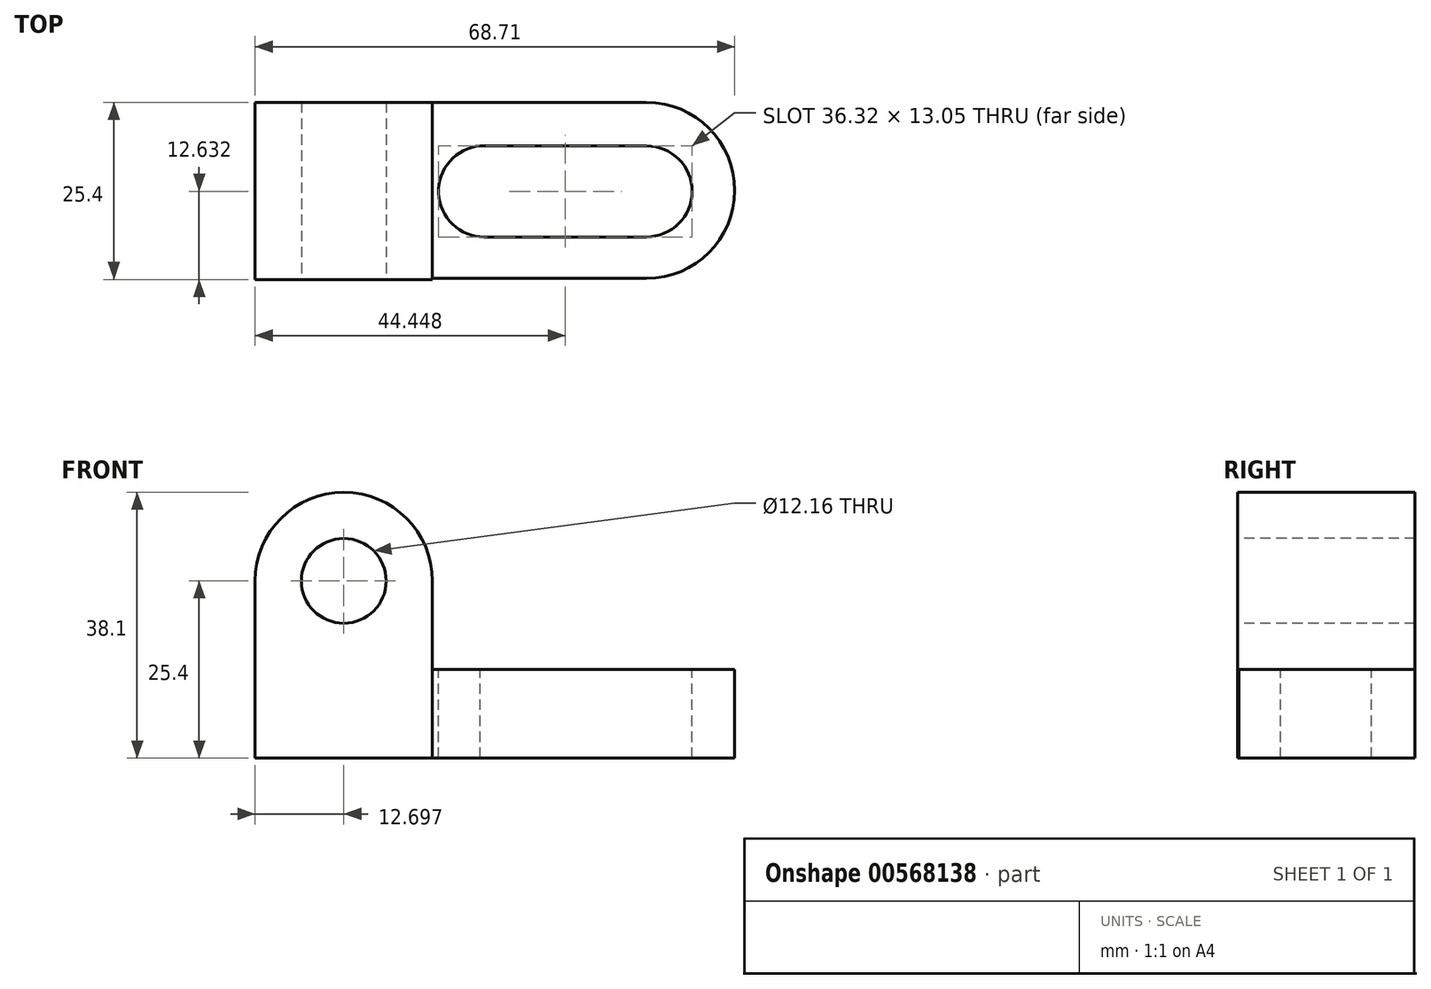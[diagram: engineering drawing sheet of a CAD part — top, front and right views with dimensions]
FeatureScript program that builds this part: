
annotation { "Feature Type Name" : "Feature", "Feature Type Description" : "" }
export const myFeature = defineFeature(function(context is Context, id is Id, definition is map)
    precondition{}
    {
        {
            var Q0;
            Q0=qCreatedBy(makeId("Front.planeOp"),FACE);
            var sketch = newSketch(context, id + "F0", { "sketchPlane" : qUnion([Q0])});
            skLineSegment(sketch, "E0", {"start": v(-70.27, 0) * mm, "end": v(-44.87, 0) * mm});
            skLineSegment(sketch, "E1", {"start": v(-44.87, 0) * mm, "end": v(-44.87, 25.4) * mm});
            skLineSegment(sketch, "E2", {"start": v(-44.87, 25.4) * mm, "end": v(-70.27, 25.4) * mm});
            skLineSegment(sketch, "E3", {"start": v(-70.27, 25.4) * mm, "end": v(-70.27, 0) * mm});
            skArc(sketch, "E4", {"start": v(-44.87, 25.4) * mm, "mid": v(-57.57, 38.1) * mm, "end": v(-70.27, 25.4) * mm});
            skSolve(sketch);
        }
        {
            var Q0;
            Q0=makeQuery(id+"F0.imprint","IMPRINT",FACE,{"disambiguationData":[TD([[makeQuery(id+"F0.imprint","IMPRINT",EDGE,{"derivedFrom":sQuery(id+"F0.wireOp",EDGE,"E0")}),1.0]])]});
            var Q1;
            Q1=makeQuery(id+"F0.imprint","IMPRINT",FACE,{"disambiguationData":[TD([[makeQuery(id+"F0.imprint","IMPRINT",EDGE,{"derivedFrom":sQuery(id+"F0.wireOp",EDGE,"E2")}),-1.0]])]});
            extrude(context, id + "F1", {"entities" : qUnion([Q0, Q1]), "depth" : 25.4 * mm, "offsetDistance" : 25.4 * mm});
        }
        {
            var Q0;
            Q0=qCreatedBy(makeId("Top.planeOp"),FACE);
            var sketch = newSketch(context, id + "F2", { "sketchPlane" : qUnion([Q0])});
            skLineSegment(sketch, "E5", {"start": v(-45.68, 0) * mm, "end": v(-45.68, -25.25) * mm});
            skLineSegment(sketch, "E6", {"start": v(-45.68, -25.25) * mm, "end": v(-14.19, -25.25) * mm});
            skLineSegment(sketch, "E7", {"start": v(-14.19, -25.25) * mm, "end": v(-14.19, 0) * mm});
            skLineSegment(sketch, "E8", {"start": v(-14.19, 0) * mm, "end": v(-45.68, 0) * mm});
            skArc(sketch, "E9", {"start": v(-14.19, -25.25) * mm, "mid": v(-1.56, -12.63) * mm, "end": v(-14.19, 0) * mm});
            skSolve(sketch);
        }
        {
            var Q0;
            Q0=makeQuery(id+"F2.imprint","IMPRINT",FACE,{"disambiguationData":[TD([[makeQuery(id+"F2.imprint","IMPRINT",EDGE,{"derivedFrom":sQuery(id+"F2.wireOp",EDGE,"E5")}),1.0]])]});
            var Q1;
            Q1=makeQuery(id+"F2.imprint","IMPRINT",FACE,{"disambiguationData":[TD([[makeQuery(id+"F2.imprint","IMPRINT",EDGE,{"derivedFrom":sQuery(id+"F2.wireOp",EDGE,"E7")}),-1.0]])]});
            extrude(context, id + "F3", {"entities" : qUnion([Q0, Q1]), "operationType" : NewBodyOperationType.ADD, "depth" : 12.7 * mm, "offsetDistance" : 25.4 * mm});
        }
        {
            var Q0;
            Q0=makeQuery(id+"F1.opExtrude","CAP_FACE",FACE,{"disambiguationData":[OSD([sQuery(id+"F0.wireOp",EDGE,"E0"),sQuery(id+"F0.wireOp",EDGE,"E1"),sQuery(id+"F0.wireOp",EDGE,"E3"),sQuery(id+"F0.wireOp",EDGE,"E4")])],"isStart":false});
            var sketch = newSketch(context, id + "F4", { "sketchPlane" : qUnion([Q0])});
            skCircle(sketch, "E10", {"center": v(-57.57, 25.4) * mm, "radius": 6.08 * mm});
            skSolve(sketch);
        }
        {
            var Q0;
            Q0=makeQuery(id+"F4.imprint","IMPRINT",FACE,{"disambiguationData":[TD([[makeQuery(id+"F4.imprint","IMPRINT",EDGE,{"derivedFrom":sQuery(id+"F4.wireOp",EDGE,"E10")}),1.0]])]});
            extrude(context, id + "F5", {"entities" : qUnion([Q0]), "operationType" : NewBodyOperationType.ADD, "depth" : 25.4 * mm, "offsetDistance" : 25.4 * mm});
        }
        {
            var Q0;
            Q0=makeQuery(id+"F5.opExtrude","CAP_FACE",FACE,{"disambiguationData":[OSD([sQuery(id+"F4.wireOp",EDGE,"E10")])],"isStart":false});
            extrude(context, id + "F6", {"entities" : qUnion([Q0]), "operationType" : NewBodyOperationType.REMOVE, "oppositeDirection" : true, "depth" : 50.8 * mm, "offsetDistance" : 25.4 * mm});
        }
        {
            var Q0;
            Q0=makeQuery(id+"F3.opExtrude","CAP_FACE",FACE,{"disambiguationData":[OSD([sQuery(id+"F2.wireOp",EDGE,"E5"),sQuery(id+"F2.wireOp",EDGE,"E6"),sQuery(id+"F2.wireOp",EDGE,"E8"),sQuery(id+"F2.wireOp",EDGE,"E9")])],"isStart":false});
            var sketch = newSketch(context, id + "F7", { "sketchPlane" : qUnion([Q0])});
            skLineSegment(sketch, "E11", {"start": v(-14.19, -6.24) * mm, "end": v(-38.02, -6.24) * mm});
            skLineSegment(sketch, "E12", {"start": v(-14.19, -19.3) * mm, "end": v(-37.45, -19.3) * mm});
            skArc(sketch, "E13", {"start": v(-14.19, -19.3) * mm, "mid": v(-7.66, -12.77) * mm, "end": v(-14.19, -6.24) * mm});
            skArc(sketch, "E14", {"start": v(-38.02, -6.24) * mm, "mid": v(-43.98, -13.04) * mm, "end": v(-37.45, -19.3) * mm});
            skSolve(sketch);
        }
        {
            var Q0;
            Q0=makeQuery(id+"F7.imprint","IMPRINT",FACE,{"disambiguationData":[TD([[makeQuery(id+"F7.imprint","IMPRINT",EDGE,{"derivedFrom":sQuery(id+"F7.wireOp",EDGE,"E11")}),1.0]])]});
            extrude(context, id + "F8", {"entities" : qUnion([Q0]), "operationType" : NewBodyOperationType.REMOVE, "oppositeDirection" : true, "depth" : 12.7 * mm, "offsetDistance" : 25.4 * mm});
        }
    });
